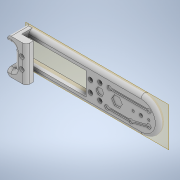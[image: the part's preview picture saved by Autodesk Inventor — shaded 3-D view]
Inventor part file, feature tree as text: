
AUTODESK INVENTOR PART (.ipt)
format: ipt  version: 2022 (Build 260153000, 153)  size: 401,408 bytes
history: native  units: in
note: dims shown in document units (in); Inventor stores cm internally (conversion verified against a paired STEP export)
features: sketch x11, extrude x9, projected_geometry x7, fillet x2, plane x1, mirror x1
ambient origin geometry x8: Origin, YZ Plane, XZ Plane, XY Plane, X Axis, Y Axis, Z Axis, Center Point
bodies: Solid1 (feature_tree)
feature tree (31):
  extrude  "Extrusion1"  Depth=0.25in
  fillet  "Fillet1"  Radius=0.25in
  extrude  "Extrusion2"  Depth=0.157in
  sketch  "Sketch3"  dims[d6=0.157in d7=0.195in]
  sketch  "Sketch4"  dims[d8=0.8in d9=1.6in]
  extrude  "Extrusion3"  Depth=0.195in
  extrude  "Extrusion4"  Depth=1.6in
  extrude  "Extrusion5"  Depth=0.275in
  extrude  "Extrusion6"  Depth=0.0787in
  plane  "Work Plane1"
  mirror  "Mirror1"
  extrude  "Extrusion7"  Depth=0.118in
  extrude  "Extrusion8"  Depth=0.125in
  extrude  "Extrusion9"  Depth=0.0984in
  fillet  "Fillet2"  Radius=0.0984in
  sketch  "Sketch1"  dims[d0=1.25in d1=3.937in d3=0.25in]
  sketch  "Sketch2"  dims[d4=0.195in d5=0.157in]
  projected_geometry  "Projected Loop1"
  projected_geometry  "Projected Loop2"
  sketch  "Sketch5"  dims[d10=0.157in d11=0.275in]
  sketch  "Sketch6"  dims[d12=0.0787in d13=0.0787in]
  sketch  "Sketch7"  dims[d14=0.275in d15=0.118in]
  projected_geometry  "Projected Loop3"
  sketch  "Sketch8"  dims[d16=0.25in d17=0.0in d18=0.125in]
  projected_geometry  "Projected Loop4"
  sketch  "Sketch9"  dims[d19=0.2362in d20=0.0984in d21=0.0984in]
  projected_geometry  "Projected Loop5"
  projected_geometry  "Projected Loop6"
  sketch  "Sketch10"  dims[d22=0.25in d23=0.0in]
  projected_geometry  "Projected Loop7"
  sketch  "Sketch11"  dims[d24=0.325in d25=1.0in d26=0.0in d27=1.0in d28=0.0in d29=0.157in d30=0.33in d31=0.0in d32=0.0in d34=0.1575in d35=0.1575in d36=0.1575in d37=0.1575in d39=0.1575in d40=0.0394in d41=0.0394in d42=0.0394in d43=0.0394in d44=0.0394in d45=0.0394in d46=0.0394in d47=0.0in d48=0.187in d49=0.0591in d50=0.125in d51=0.25in d52=0.0in d53=0.25in d54=0.5in d55=0.0in d56=0.407in d57=0.157in d58=0.25in d59=0.43in d60=0.25in d61=0.0in d62=0.125in]
